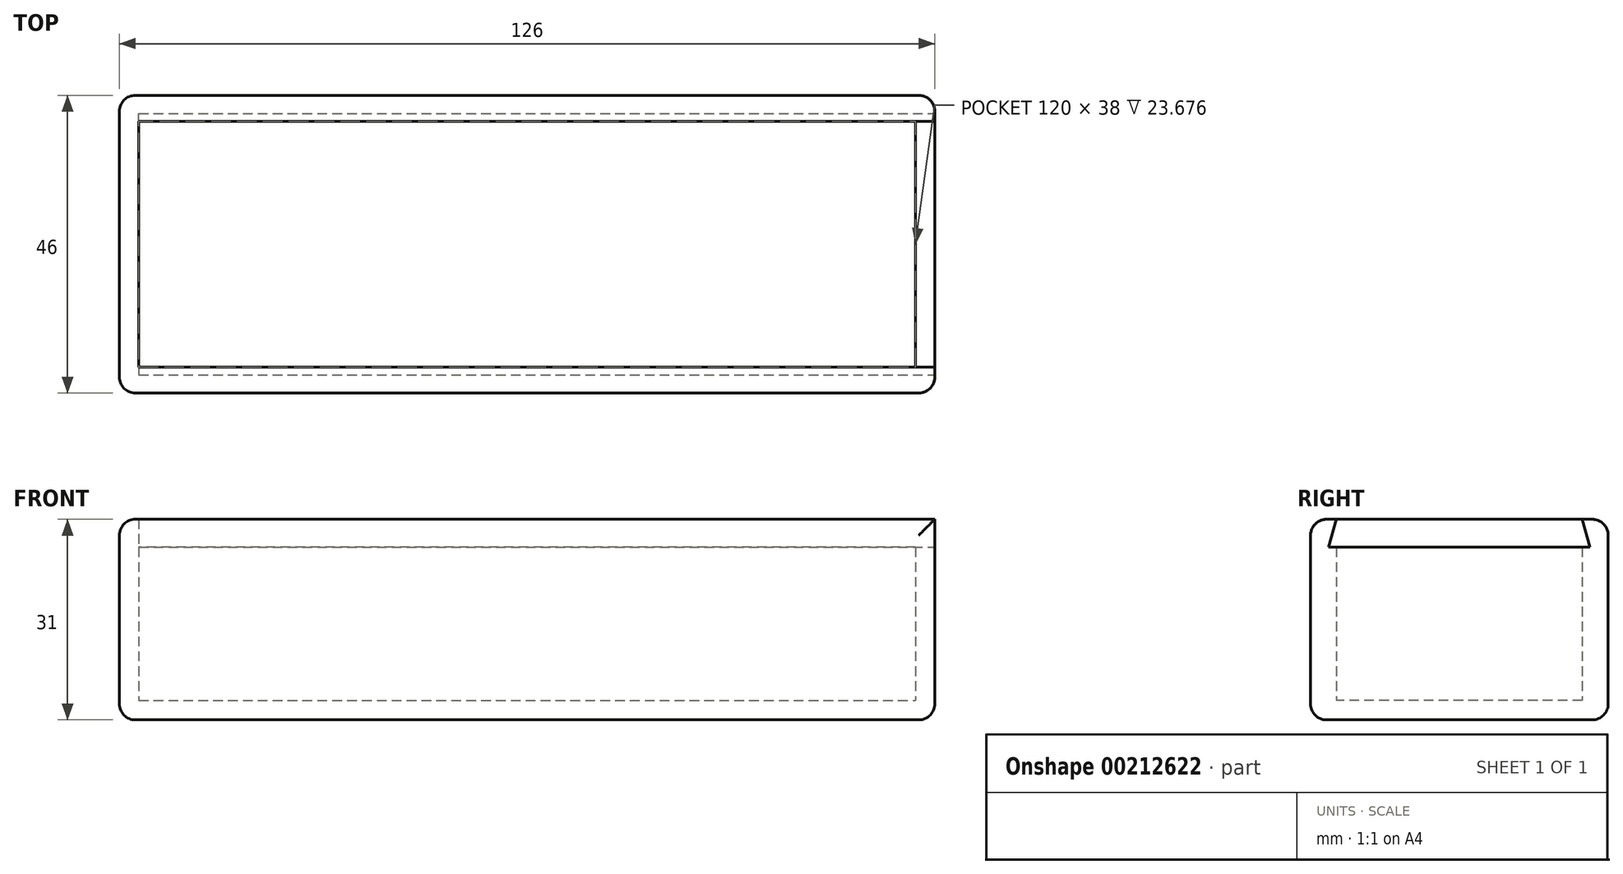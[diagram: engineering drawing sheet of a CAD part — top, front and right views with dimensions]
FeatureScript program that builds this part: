
annotation { "Feature Type Name" : "Feature", "Feature Type Description" : "" }
export const myFeature = defineFeature(function(context is Context, id is Id, definition is map)
    precondition{}
    {
        {
            var Q0;
            Q0=qCreatedBy(makeId("Top.planeOp"),FACE);
            var sketch = newSketch(context, id + "F0", { "sketchPlane" : qUnion([Q0])});
            skLineSegment(sketch, "E0.bottom", {"start": v(-62.87, 13.22) * mm, "end": v(63.13, 13.22) * mm});
            skLineSegment(sketch, "E0.top", {"start": v(-62.87, -32.78) * mm, "end": v(63.13, -32.78) * mm});
            skLineSegment(sketch, "E0.left", {"start": v(-62.87, 13.22) * mm, "end": v(-62.87, -32.78) * mm});
            skLineSegment(sketch, "E0.right", {"start": v(63.13, 13.22) * mm, "end": v(63.13, -32.78) * mm});
            skLineSegment(sketch, "E1.bottom", {"start": v(-59.87, 9.22) * mm, "end": v(60.13, 9.22) * mm});
            skLineSegment(sketch, "E1.top", {"start": v(-59.87, -28.78) * mm, "end": v(60.13, -28.78) * mm});
            skLineSegment(sketch, "E1.left", {"start": v(-59.87, 9.22) * mm, "end": v(-59.87, -28.78) * mm});
            skLineSegment(sketch, "E1.right", {"start": v(60.13, 9.22) * mm, "end": v(60.13, -28.78) * mm});
            skSolve(sketch);
        }
        {
            var Q0;
            Q0=makeQuery(id+"F0.imprint","IMPRINT",FACE,{"disambiguationData":[TD([[makeQuery(id+"F0.imprint","IMPRINT",EDGE,{"derivedFrom":sQuery(id+"F0.wireOp",EDGE,"E0.bottom")}),-1.0]])]});
            var Q1;
            Q1=makeQuery(id+"F0.imprint","IMPRINT",FACE,{"disambiguationData":[TD([[makeQuery(id+"F0.imprint","IMPRINT",EDGE,{"derivedFrom":sQuery(id+"F0.wireOp",EDGE,"E1.bottom")}),-1.0]])]});
            extrude(context, id + "F1", {"entities" : qUnion([Q0, Q1]), "oppositeDirection" : true, "depth" : 3 * mm});
        }
        {
            var Q0;
            Q0=makeQuery(id+"F0.imprint","IMPRINT",FACE,{"disambiguationData":[TD([[makeQuery(id+"F0.imprint","IMPRINT",EDGE,{"derivedFrom":sQuery(id+"F0.wireOp",EDGE,"E0.bottom")}),-1.0]])]});
            extrude(context, id + "F2", {"entities" : qUnion([Q0]), "operationType" : NewBodyOperationType.ADD, "depth" : 28 * mm});
        }
        {
            var Q0;
            {var subQ0=sQuery(id+"F0.wireOp",EDGE,"E0.right");Q0=makeQuery(id+"F2.boolean.opBoolean","MERGE",FACE,{"derivedFrom":[makeQuery(id+"F1.opExtrude","SWEPT_FACE",FACE,{"disambiguationData":[OSD([subQ0])]}),makeQuery(id+"F2.opExtrude","SWEPT_FACE",FACE,{"disambiguationData":[OSD([subQ0])]})]});}
            var sketch = newSketch(context, id + "F3", { "sketchPlane" : qUnion([Q0])});
            skLineSegment(sketch, "E2.bottom", {"start": v(-28.78, 28) * mm, "end": v(9.22, 28) * mm});
            skLineSegment(sketch, "E2.top", {"start": v(-28.78, 23.68) * mm, "end": v(9.22, 23.68) * mm});
            skLineSegment(sketch, "E3", {"start": v(-28.78, 28) * mm, "end": v(-29.98, 23.68) * mm});
            skLineSegment(sketch, "E4", {"start": v(-29.98, 23.68) * mm, "end": v(-28.78, 23.68) * mm});
            skLineSegment(sketch, "E5", {"start": v(9.22, 28) * mm, "end": v(10.42, 23.68) * mm});
            skLineSegment(sketch, "E6", {"start": v(10.42, 23.68) * mm, "end": v(9.22, 23.68) * mm});
            skSolve(sketch);
        }
        {
            var Q0;
            Q0=makeQuery(id+"F3.imprint","IMPRINT",FACE,{"disambiguationData":[TD([[makeQuery(id+"F3.imprint","IMPRINT",EDGE,{"derivedFrom":sQuery(id+"F3.wireOp",EDGE,"E2.bottom")}),1.0]])]});
            extrude(context, id + "F4", {"entities" : qUnion([Q0]), "operationType" : NewBodyOperationType.REMOVE, "oppositeDirection" : true, "depth" : 123 * mm});
        }
        {
            var Q0;
            {var subQ0=sQuery(id+"F0.wireOp",EDGE,"E0.right");var subQ1=sQuery(id+"F0.wireOp",EDGE,"E0.top");Q0=makeQuery(id+"F2.boolean.opBoolean","MERGE",EDGE,{"derivedFrom":[makeQuery(id+"F1.opExtrude","SWEPT_EDGE",EDGE,{"disambiguationData":[OSD([subQ1,subQ0])]}),makeQuery(id+"F2.opExtrude","SWEPT_EDGE",EDGE,{"disambiguationData":[OSD([subQ1,subQ0])]})]});}
            var Q1;
            {var subQ0=sQuery(id+"F0.wireOp",EDGE,"E0.right");var subQ1=sQuery(id+"F0.wireOp",EDGE,"E0.bottom");Q1=makeQuery(id+"F2.boolean.opBoolean","MERGE",EDGE,{"derivedFrom":[makeQuery(id+"F1.opExtrude","SWEPT_EDGE",EDGE,{"disambiguationData":[OSD([subQ1,subQ0])]}),makeQuery(id+"F2.opExtrude","SWEPT_EDGE",EDGE,{"disambiguationData":[OSD([subQ1,subQ0])]})]});}
            var Q2;
            {var subQ0=sQuery(id+"F0.wireOp",EDGE,"E0.left");var subQ1=sQuery(id+"F0.wireOp",EDGE,"E0.top");Q2=makeQuery(id+"F2.boolean.opBoolean","MERGE",EDGE,{"derivedFrom":[makeQuery(id+"F1.opExtrude","SWEPT_EDGE",EDGE,{"disambiguationData":[OSD([subQ1,subQ0])]}),makeQuery(id+"F2.opExtrude","SWEPT_EDGE",EDGE,{"disambiguationData":[OSD([subQ1,subQ0])]})]});}
            var Q3;
            {var subQ0=sQuery(id+"F0.wireOp",EDGE,"E0.left");var subQ1=sQuery(id+"F0.wireOp",EDGE,"E0.bottom");Q3=makeQuery(id+"F2.boolean.opBoolean","MERGE",EDGE,{"derivedFrom":[makeQuery(id+"F1.opExtrude","SWEPT_EDGE",EDGE,{"disambiguationData":[OSD([subQ1,subQ0])]}),makeQuery(id+"F2.opExtrude","SWEPT_EDGE",EDGE,{"disambiguationData":[OSD([subQ1,subQ0])]})]});}
            var Q4;
            Q4=makeQuery(id+"F1.opExtrude","CAP_EDGE",EDGE,{"disambiguationData":[OSD([sQuery(id+"F0.wireOp",EDGE,"E0.bottom")])],"isStart":false});
            var Q5;
            Q5=makeQuery(id+"F1.opExtrude","CAP_EDGE",EDGE,{"disambiguationData":[OSD([sQuery(id+"F0.wireOp",EDGE,"E0.right")])],"isStart":false});
            var Q6;
            Q6=makeQuery(id+"F1.opExtrude","CAP_EDGE",EDGE,{"disambiguationData":[OSD([sQuery(id+"F0.wireOp",EDGE,"E0.top")])],"isStart":false});
            var Q7;
            Q7=makeQuery(id+"F1.opExtrude","CAP_EDGE",EDGE,{"disambiguationData":[OSD([sQuery(id+"F0.wireOp",EDGE,"E0.left")])],"isStart":false});
            var Q8;
            Q8=makeQuery(id+"F2.opExtrude","CAP_EDGE",EDGE,{"disambiguationData":[OSD([sQuery(id+"F0.wireOp",EDGE,"E0.top")])],"isStart":false});
            var Q9;
            Q9=makeQuery(id+"F2.opExtrude","CAP_EDGE",EDGE,{"disambiguationData":[OSD([sQuery(id+"F0.wireOp",EDGE,"E0.left")])],"isStart":false});
            var Q10;
            Q10=makeQuery(id+"F2.opExtrude","CAP_EDGE",EDGE,{"disambiguationData":[OSD([sQuery(id+"F0.wireOp",EDGE,"E0.bottom")])],"isStart":false});
            fillet(context, id + "F5", {"entities" : qUnion([Q0, Q1, Q2, Q3, Q4, Q5, Q6, Q7, Q8, Q9, Q10]), "radius" : 2.5 * mm, "tangentPropagation" : true, "allowEdgeOverflow" : false});
        }
    });
